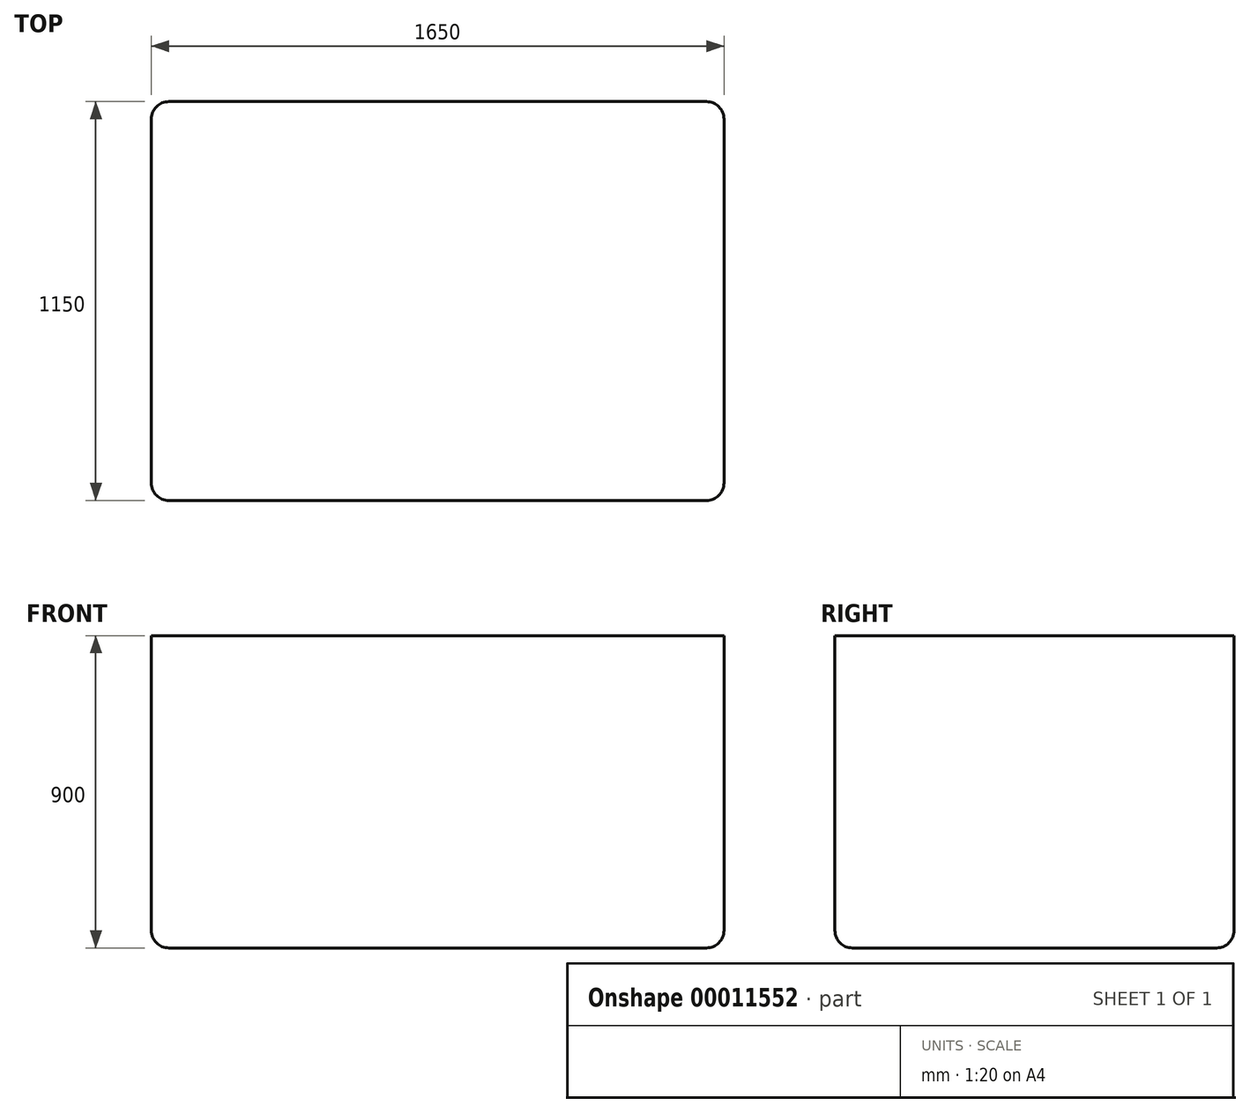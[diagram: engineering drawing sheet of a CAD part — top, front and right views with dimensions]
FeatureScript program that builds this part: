
annotation { "Feature Type Name" : "Feature", "Feature Type Description" : "" }
export const myFeature = defineFeature(function(context is Context, id is Id, definition is map)
    precondition{}
    {
        {
            var Q0;
            Q0=qCreatedBy(makeId("Top.planeOp"),FACE);
            var sketch = newSketch(context, id + "F0", { "sketchPlane" : qUnion([Q0])});
            skLineSegment(sketch, "E0.rect.bottom", {"start": v(825, 570.27) * mm, "end": v(-825, 570.27) * mm});
            skLineSegment(sketch, "E0.rect.top", {"start": v(825, -579.73) * mm, "end": v(-825, -579.73) * mm});
            skLineSegment(sketch, "E0.rect.left", {"start": v(825, 570.27) * mm, "end": v(825, -579.73) * mm});
            skLineSegment(sketch, "E0.rect.right", {"start": v(-825, 570.27) * mm, "end": v(-825, -579.73) * mm});
            skPoint(sketch, "E0.rect.middle", {"position": v(0, -4.73) * mm});
            skSolve(sketch);
        }
        {
            var Q0;
            Q0=makeQuery(id+"F0.imprint","IMPRINT",FACE,{"disambiguationData":[TD([[makeQuery(id+"F0.imprint","IMPRINT",EDGE,{"derivedFrom":sQuery(id+"F0.wireOp",EDGE,"E0.rect.bottom")}),1.0]])]});
            extrude(context, id + "F1", {"entities" : qUnion([Q0]), "depth" : 900 * mm});
        }
        {
            var Q0;
            Q0=makeQuery(id+"F1.opExtrude","SWEPT_EDGE",EDGE,{"disambiguationData":[OSD([sQuery(id+"F0.wireOp",EDGE,"E0.rect.top"),sQuery(id+"F0.wireOp",EDGE,"E0.rect.left")])]});
            var Q1;
            Q1=makeQuery(id+"F1.opExtrude","SWEPT_EDGE",EDGE,{"disambiguationData":[OSD([sQuery(id+"F0.wireOp",EDGE,"E0.rect.bottom"),sQuery(id+"F0.wireOp",EDGE,"E0.rect.left")])]});
            var Q2;
            Q2=makeQuery(id+"F1.opExtrude","SWEPT_EDGE",EDGE,{"disambiguationData":[OSD([sQuery(id+"F0.wireOp",EDGE,"E0.rect.top"),sQuery(id+"F0.wireOp",EDGE,"E0.rect.right")])]});
            var Q3;
            Q3=makeQuery(id+"F1.opExtrude","SWEPT_EDGE",EDGE,{"disambiguationData":[OSD([sQuery(id+"F0.wireOp",EDGE,"E0.rect.bottom"),sQuery(id+"F0.wireOp",EDGE,"E0.rect.right")])]});
            fillet(context, id + "F2", {"entities" : qUnion([Q0, Q1, Q2, Q3]), "radius" : 50 * mm, "tangentPropagation" : true, "allowEdgeOverflow" : false});
        }
        {
            var Q0;
            Q0=makeQuery(id+"F1.opExtrude","CAP_EDGE",EDGE,{"disambiguationData":[OSD([sQuery(id+"F0.wireOp",EDGE,"E0.rect.top")])],"isStart":true});
            fillet(context, id + "F3", {"entities" : qUnion([Q0]), "radius" : 50 * mm, "tangentPropagation" : true, "allowEdgeOverflow" : false});
        }
    });
